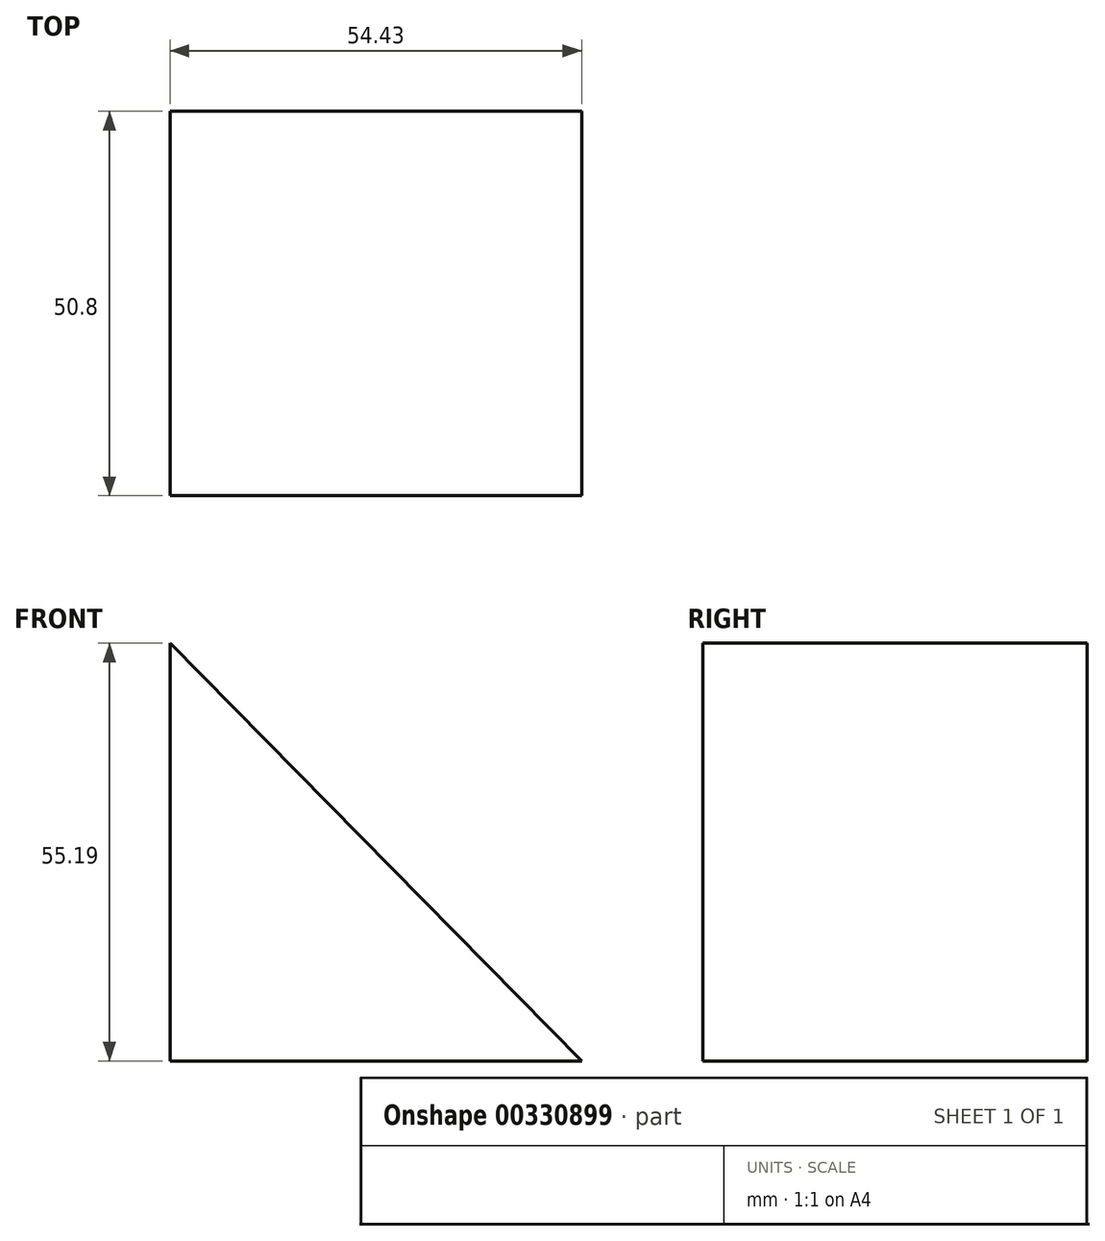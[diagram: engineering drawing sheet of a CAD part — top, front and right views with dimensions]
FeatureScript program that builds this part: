
annotation { "Feature Type Name" : "Feature", "Feature Type Description" : "" }
export const myFeature = defineFeature(function(context is Context, id is Id, definition is map)
    precondition{}
    {
        {
            var Q0;
            Q0=qCreatedBy(makeId("Front.planeOp"),FACE);
            var sketch = newSketch(context, id + "F0", { "sketchPlane" : qUnion([Q0])});
            skLineSegment(sketch, "E0", {"start": v(-41.13, 55.2) * mm, "end": v(-41.13, 0) * mm});
            skLineSegment(sketch, "E1", {"start": v(-41.13, 0) * mm, "end": v(13.3, 0) * mm});
            skLineSegment(sketch, "E2", {"start": v(13.3, 0) * mm, "end": v(-41.13, 55.2) * mm});
            skSolve(sketch);
        }
        {
            var Q0;
            Q0 = qSketchRegion(id + "F0", true);
            extrude(context, id + "F1", {"entities" : qUnion([Q0]), "depth" : 50.8 * mm});
        }
    });
